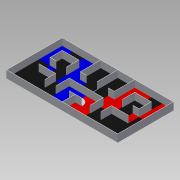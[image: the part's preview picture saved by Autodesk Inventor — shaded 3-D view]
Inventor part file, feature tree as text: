
AUTODESK INVENTOR PART (.ipt)
format: ipt  version: 2015 SP1 (Build 190203100, 203)  size: 415,744 bytes
history: native  units: mm
features: extrude x7, sketch x5, mirror x1, plane x1
ambient origin geometry x8: Origin, YZ Plane, XZ Plane, XY Plane, X Axis, Y Axis, Z Axis, Center Point
bodies: Solid1 (feature_tree)
feature tree (14):
  sketch  "Sketch1"  dims[d2=20.0mm d51=460.0mm d52=460.0mm]
  extrude  "Extrusion1"  Depth=460.0mm
  extrude  "Extrusion2"  Depth=320.0mm TaperAngle=0.0deg
  extrude  "Extrusion3"  Depth=0.001mm TaperAngle=0.0deg
  mirror  "Mirror1"
  extrude  "Extrusion4"  Depth=0.001mm TaperAngle=0.0deg
  sketch  "Sketch5"  dims[d185=460.0mm d186=0.001mm d187=0.0mm]
  extrude  "Extrusion5"  Depth=300.0mm TaperAngle=0.0deg
  extrude  "Extrusion6"  Depth=20.0mm
  extrude  "Extrusion7"  Depth=460.0mm
  plane  "Work Plane1"
  sketch  "Sketch3"  dims[d97=20.0mm d98=0.0mm d99=320.0mm d100=0.0mm]
  sketch  "Sketch4"  dims[d181=260.0mm d183=0.001mm d184=0.0mm]
  sketch  "Sketch6"  dims[d190=20.0mm d191=300.0mm d192=0.0mm d193=20.0mm d194=460.0mm d195=0.001mm d196=0.0mm d197=600.0mm d198=4.0mm d199=0.0mm d274=4860.0mm d275=2440.0mm d276=2400.0mm d277=2400.0mm d278=720.0mm d279=450.0mm d280=20.0mm d281=470.0mm d282=740.0mm d283=20.0mm d284=700.0mm d285=510.0mm d286=260.0mm d287=20.0mm d288=280.0mm d289=550.0mm d290=740.0mm d291=550.0mm d292=20.0mm d293=530.0mm d294=890.0mm d295=280.0mm d296=20.0mm d297=260.0mm d298=870.0mm d300=870.0mm d301=20.0mm d302=550.0mm d303=260.0mm d304=20.0mm d305=540.0mm d306=570.0mm d307=20.0mm d308=590.0mm d309=1500.0mm d310=1460.0mm d311=2400.0mm d312=20.0mm d313=20.0mm d314=20.0mm d315=20.0mm d316=20.0mm d318=1660.0mm d319=20.0mm d320=720.0mm d324=20.0mm d330=720.0mm d331=740.0mm d332=470.0mm d333=20.0mm d334=20.0mm d336=530.0mm d337=510.0mm d338=260.0mm d339=20.0mm d341=550.0mm d343=550.0mm d346=870.0mm d352=460.0mm d353=460.0mm d356=460.0mm d358=460.0mm d359=460.0mm d364=460.0mm d365=460.0mm d366=460.0mm d367=460.0mm d368=460.0mm d369=480.0mm d370=460.0mm d371=460.0mm d372=460.0mm d374=910.0mm d375=20.0mm]
